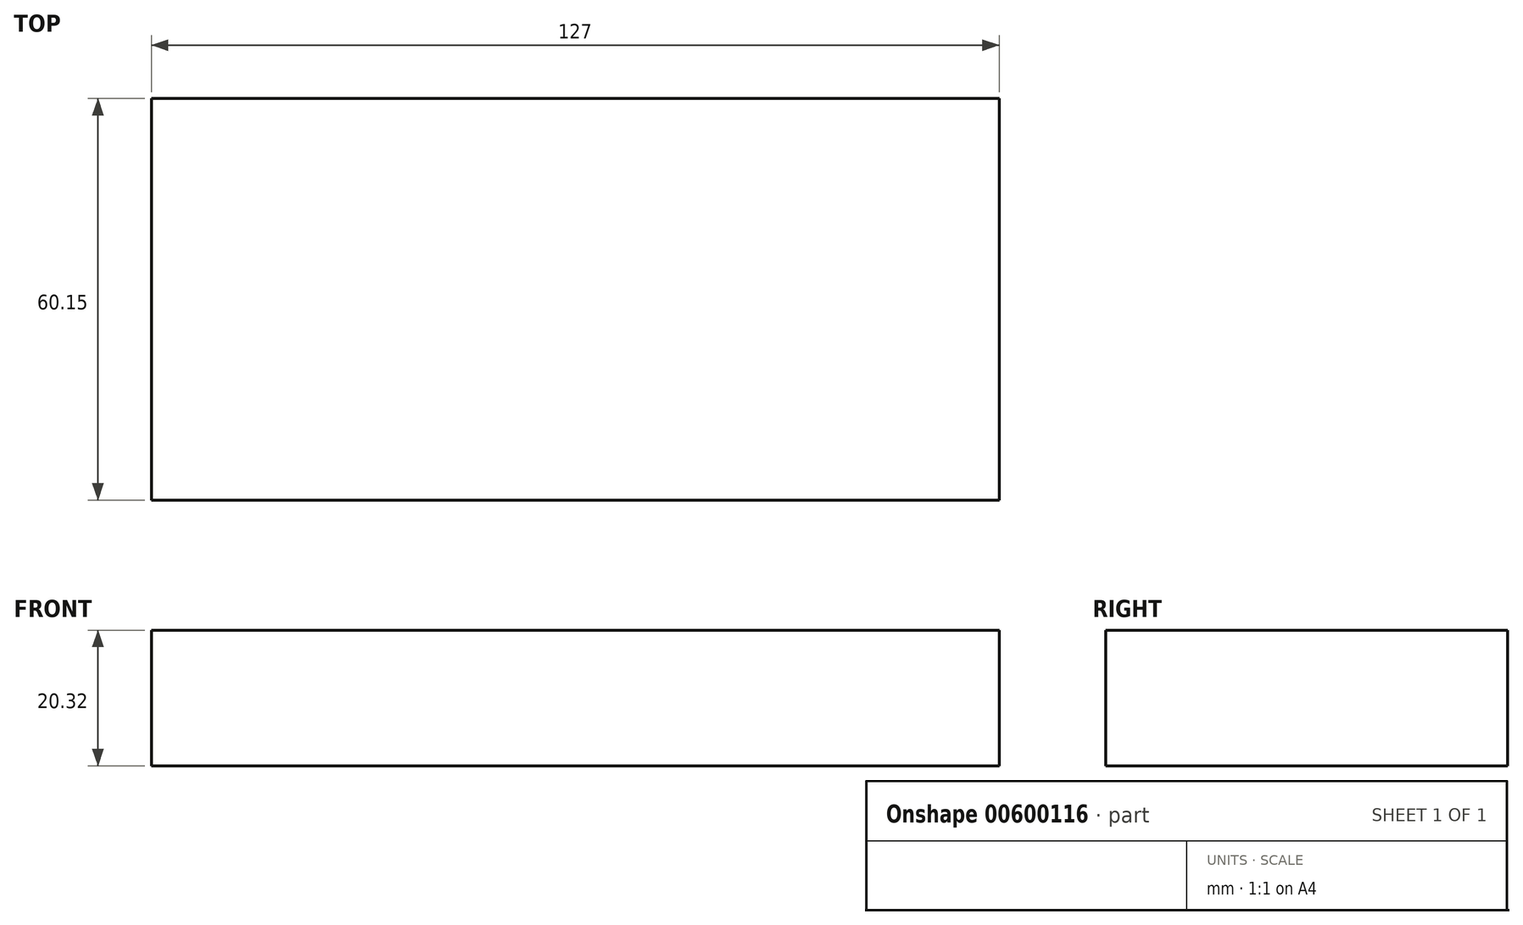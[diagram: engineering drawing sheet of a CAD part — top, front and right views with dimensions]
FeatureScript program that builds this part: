
annotation { "Feature Type Name" : "Feature", "Feature Type Description" : "" }
export const myFeature = defineFeature(function(context is Context, id is Id, definition is map)
    precondition{}
    {
        {
            var Q0;
            Q0=qCreatedBy(makeId("Top.planeOp"),FACE);
            var sketch = newSketch(context, id + "F0", { "sketchPlane" : qUnion([Q0])});
            skLineSegment(sketch, "E0.bottom", {"start": v(-54.66, 27.75) * mm, "end": v(72.34, 27.75) * mm});
            skLineSegment(sketch, "E0.top", {"start": v(-54.66, -32.4) * mm, "end": v(72.34, -32.4) * mm});
            skLineSegment(sketch, "E0.left", {"start": v(-54.66, 27.75) * mm, "end": v(-54.66, -32.4) * mm});
            skLineSegment(sketch, "E0.right", {"start": v(72.34, 27.75) * mm, "end": v(72.34, -32.4) * mm});
            skSolve(sketch);
        }
        {
            var Q0;
            Q0 = qSketchRegion(id + "F0", true);
            extrude(context, id + "F1", {"entities" : qUnion([Q0]), "depth" : 20.32 * mm, "offsetDistance" : 25.4 * mm});
        }
    });
